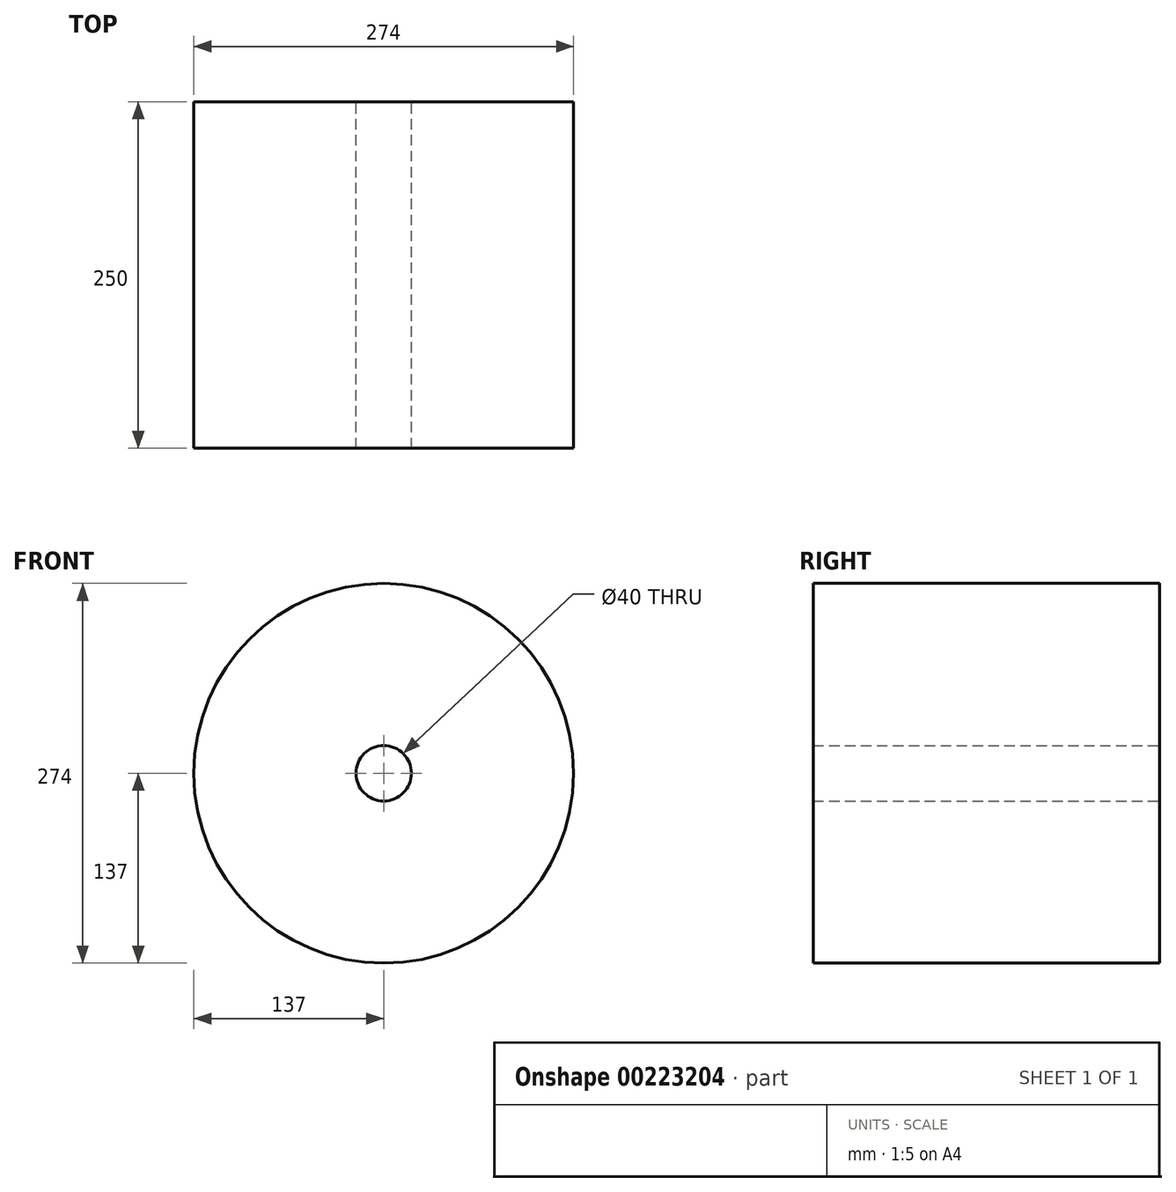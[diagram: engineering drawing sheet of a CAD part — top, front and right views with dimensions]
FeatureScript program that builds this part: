
annotation { "Feature Type Name" : "Feature", "Feature Type Description" : "" }
export const myFeature = defineFeature(function(context is Context, id is Id, definition is map)
    precondition{}
    {
        {
            var Q0;
            Q0=qCreatedBy(makeId("Front.planeOp"),FACE);
            var sketch = newSketch(context, id + "F0", { "sketchPlane" : qUnion([Q0])});
            skCircle(sketch, "E0", {"center": v(0, 0) * mm, "radius": 137 * mm});
            skCircle(sketch, "E1", {"center": v(0, 0) * mm, "radius": 20 * mm});
            skSolve(sketch);
        }
        {
            var Q0;
            Q0=makeQuery(id+"F0.imprint","IMPRINT",FACE,{"disambiguationData":[TD([[makeQuery(id+"F0.imprint","IMPRINT",EDGE,{"derivedFrom":sQuery(id+"F0.wireOp",EDGE,"E0")}),1.0]])]});
            extrude(context, id + "F1", {"entities" : qUnion([Q0]), "depth" : 250 * mm});
        }
    });
